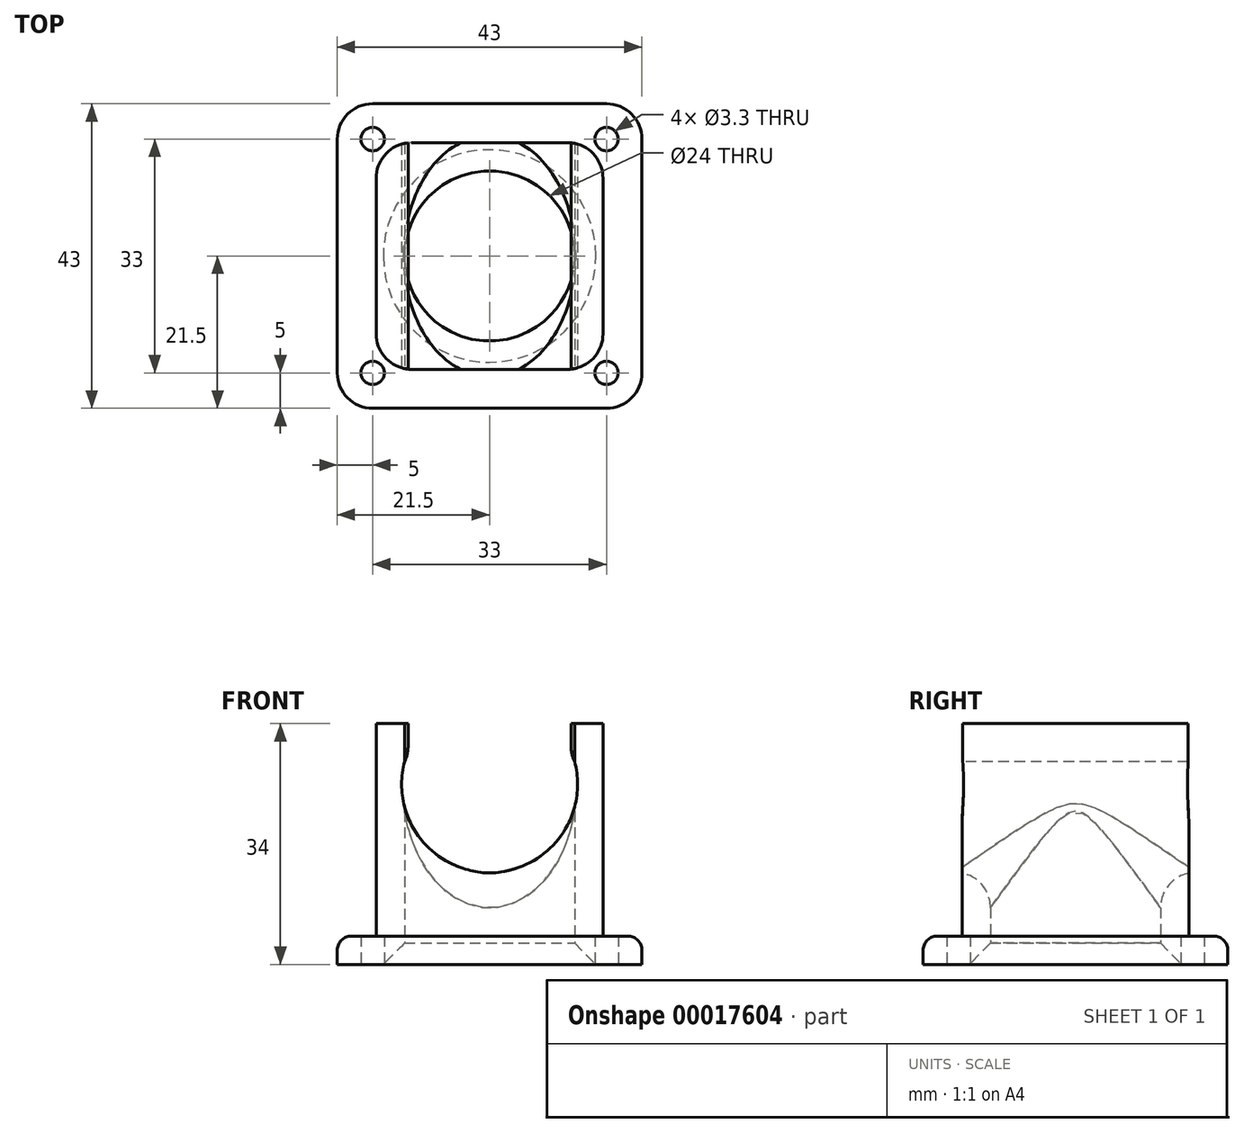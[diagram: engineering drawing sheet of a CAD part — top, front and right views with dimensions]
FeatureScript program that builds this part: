
annotation { "Feature Type Name" : "Feature", "Feature Type Description" : "" }
export const myFeature = defineFeature(function(context is Context, id is Id, definition is map)
    precondition{}
    {
        {
            var Q0;
            Q0=qCreatedBy(makeId("Top.planeOp"),FACE);
            var sketch = newSketch(context, id + "F0", { "sketchPlane" : qUnion([Q0])});
            skLineSegment(sketch, "E0.bottom", {"start": v(0, 0) * mm, "end": v(43, 0) * mm});
            skLineSegment(sketch, "E0.top", {"start": v(0, 43) * mm, "end": v(43, 43) * mm});
            skLineSegment(sketch, "E0.left", {"start": v(0, 0) * mm, "end": v(0, 43) * mm});
            skLineSegment(sketch, "E0.right", {"start": v(43, 0) * mm, "end": v(43, 43) * mm});
            skSolve(sketch);
        }
        {
            var Q0;
            Q0=qSketchRegion(id+"F0",true);
            extrude(context, id + "F1", {"entities" : qUnion([Q0]), "depth" : 4 * mm});
        }
        {
            var Q0;
            Q0=makeQuery(id+"F1.opExtrude","CAP_FACE",FACE,{"disambiguationData":[OSD([sQuery(id+"F0.wireOp",EDGE,"E0.bottom"),sQuery(id+"F0.wireOp",EDGE,"E0.top"),sQuery(id+"F0.wireOp",EDGE,"E0.left"),sQuery(id+"F0.wireOp",EDGE,"E0.right")])],"isStart":false});
            var sketch = newSketch(context, id + "F2", { "sketchPlane" : qUnion([Q0])});
            skLineSegment(sketch, "E1.bottom", {"start": v(5.5, 37.5) * mm, "end": v(37.5, 37.5) * mm});
            skLineSegment(sketch, "E1.top", {"start": v(5.5, 5.5) * mm, "end": v(37.5, 5.5) * mm});
            skLineSegment(sketch, "E1.left", {"start": v(5.5, 37.5) * mm, "end": v(5.5, 5.5) * mm});
            skLineSegment(sketch, "E1.right", {"start": v(37.5, 37.5) * mm, "end": v(37.5, 5.5) * mm});
            skLineSegment(sketch, "E2", {"start": v(21.5, 37.5) * mm, "end": v(21.5, 43) * mm});
            skLineSegment(sketch, "E3", {"start": v(37.5, 21.5) * mm, "end": v(43, 21.5) * mm});
            skSolve(sketch);
        }
        {
            var Q0;
            Q0=qSketchRegion(id+"F2",true);
            extrude(context, id + "F3", {"entities" : qUnion([Q0]), "operationType" : NewBodyOperationType.ADD, "depth" : 30 * mm});
        }
        {
            var Q0;
            Q0=makeQuery(id+"F1.opExtrude","CAP_FACE",FACE,{"disambiguationData":[OSD([sQuery(id+"F0.wireOp",EDGE,"E0.bottom"),sQuery(id+"F0.wireOp",EDGE,"E0.top"),sQuery(id+"F0.wireOp",EDGE,"E0.left"),sQuery(id+"F0.wireOp",EDGE,"E0.right")])],"isStart":true});
            var sketch = newSketch(context, id + "F4", { "sketchPlane" : qUnion([Q0])});
            skCircle(sketch, "E4", {"center": v(21.5, -21.5) * mm, "radius": 18 * mm});
            skLineSegment(sketch, "E5", {"start": v(21.5, -21.5) * mm, "end": v(21.5, 0) * mm});
            skLineSegment(sketch, "E6", {"start": v(21.5, -21.5) * mm, "end": v(43, -21.5) * mm});
            skSolve(sketch);
        }
        {
            var Q0;
            Q0=qSketchRegion(id+"F4",true);
            extrude(context, id + "F5", {"entities" : qUnion([Q0]), "operationType" : NewBodyOperationType.REMOVE, "oppositeDirection" : true, "depth" : 3 * mm});
        }
        {
            var Q0;
            Q0=makeQuery(id+"F5.boolean.opBoolean","COPY",FACE,{"derivedFrom":makeQuery(id+"F5.opExtrude","CAP_FACE",FACE,{"disambiguationData":[OSD([sQuery(id+"F4.wireOp",EDGE,"E4")])],"isStart":false})});
            var sketch = newSketch(context, id + "F6", { "sketchPlane" : qUnion([Q0])});
            skCircle(sketch, "E7", {"center": v(21.5, -21.5) * mm, "radius": 12 * mm});
            skSolve(sketch);
        }
        {
            var Q0;
            Q0=qSketchRegion(id+"F6",true);
            extrude(context, id + "F7", {"entities" : qUnion([Q0]), "operationType" : NewBodyOperationType.REMOVE, "endBound" : BoundingType.THROUGH_ALL, "oppositeDirection" : true, "depth" : 25 * mm});
        }
        {
            var Q0;
            Q0=makeQuery(id+"F3.opExtrude","SWEPT_FACE",FACE,{"disambiguationData":[OSD([sQuery(id+"F2.wireOp",EDGE,"E1.top")])]});
            var sketch = newSketch(context, id + "F8", { "sketchPlane" : qUnion([Q0])});
            skLineSegment(sketch, "E8", {"start": v(9.5, 34) * mm, "end": v(9.5, 28.62) * mm});
            skLineSegment(sketch, "E9", {"start": v(33.5, 34) * mm, "end": v(33.5, 28.62) * mm});
            skLineSegment(sketch, "E10", {"start": v(9.5, 28.62) * mm, "end": v(5.5, 28.62) * mm, "construction": true});
            skLineSegment(sketch, "E11", {"start": v(33.5, 28.62) * mm, "end": v(37.5, 28.62) * mm, "construction": true});
            skCircle(sketch, "E12", {"center": v(21.5, 25.42) * mm, "radius": 12.42 * mm});
            skSolve(sketch);
        }
        {
            var Q0;
            Q0=qSketchRegion(id+"F8",true);
            var Q1;
            {var subQ3=sQuery(id+"F8.wireOp",EDGE,"E8");Q1=makeQuery(id+"F8.imprint","IMPRINT",FACE,{"disambiguationData":[TD([[makeQuery(id+"F8.imprint","IMPRINT",EDGE,{"derivedFrom":subQ3}),1.0]])]});}
            var Q2;
            {var subQ3=sQuery(id+"F8.wireOp",EDGE,"E9");Q2=makeQuery(id+"F8.imprint","IMPRINT",FACE,{"disambiguationData":[TD([[makeQuery(id+"F8.imprint","IMPRINT",EDGE,{"derivedFrom":subQ3}),-1.0]])]});}
            extrude(context, id + "F9", {"entities" : qUnion([Q0, Q1, Q2]), "operationType" : NewBodyOperationType.REMOVE, "endBound" : BoundingType.THROUGH_ALL, "oppositeDirection" : true, "depth" : 25 * mm});
        }
        {
            var Q0;
            Q0=makeQuery(id+"F1.opExtrude","SWEPT_EDGE",EDGE,{"disambiguationData":[OSD([sQuery(id+"F0.wireOp",EDGE,"E0.top"),sQuery(id+"F0.wireOp",EDGE,"E0.right")])]});
            var Q1;
            Q1=makeQuery(id+"F1.opExtrude","SWEPT_EDGE",EDGE,{"disambiguationData":[OSD([sQuery(id+"F0.wireOp",EDGE,"E0.top"),sQuery(id+"F0.wireOp",EDGE,"E0.left")])]});
            var Q2;
            Q2=makeQuery(id+"F1.opExtrude","SWEPT_EDGE",EDGE,{"disambiguationData":[OSD([sQuery(id+"F0.wireOp",EDGE,"E0.bottom"),sQuery(id+"F0.wireOp",EDGE,"E0.left")])]});
            var Q3;
            Q3=makeQuery(id+"F1.opExtrude","SWEPT_EDGE",EDGE,{"disambiguationData":[OSD([sQuery(id+"F0.wireOp",EDGE,"E0.bottom"),sQuery(id+"F0.wireOp",EDGE,"E0.right")])]});
            fillet(context, id + "F10", {"entities" : qUnion([Q0, Q1, Q2, Q3]), "radius" : 5 * mm, "tangentPropagation" : true, "allowEdgeOverflow" : false});
        }
        {
            var Q0;
            Q0=makeQuery(id+"F3.opExtrude","CAP_EDGE",EDGE,{"disambiguationData":[OSD([sQuery(id+"F2.wireOp",EDGE,"E1.bottom")])],"isStart":true});
            var Q1;
            Q1=makeQuery(id+"F3.opExtrude","CAP_EDGE",EDGE,{"disambiguationData":[OSD([sQuery(id+"F2.wireOp",EDGE,"E1.left")])],"isStart":true});
            var Q2;
            Q2=makeQuery(id+"F3.opExtrude","CAP_EDGE",EDGE,{"disambiguationData":[OSD([sQuery(id+"F2.wireOp",EDGE,"E1.top")])],"isStart":true});
            var Q3;
            Q3=makeQuery(id+"F1.opExtrude","CAP_EDGE",EDGE,{"disambiguationData":[OSD([sQuery(id+"F0.wireOp",EDGE,"E0.bottom")])],"isStart":false});
            var Q4;
            Q4=makeQuery(id+"F1.opExtrude","CAP_EDGE",EDGE,{"disambiguationData":[OSD([sQuery(id+"F0.wireOp",EDGE,"E0.left")])],"isStart":false});
            var Q5;
            Q5=makeQuery(id+"F1.opExtrude","CAP_EDGE",EDGE,{"disambiguationData":[OSD([sQuery(id+"F0.wireOp",EDGE,"E0.top")])],"isStart":false});
            fillet(context, id + "F11", {"entities" : qUnion([Q0, Q1, Q2, Q3, Q4, Q5]), "radius" : 2 * mm, "tangentPropagation" : true, "allowEdgeOverflow" : false});
        }
        {
            var Q0;
            Q0=makeQuery(id+"F3.opExtrude","SWEPT_EDGE",EDGE,{"disambiguationData":[OSD([sQuery(id+"F2.wireOp",EDGE,"E1.top"),sQuery(id+"F2.wireOp",EDGE,"E1.left")])]});
            var Q1;
            Q1=makeQuery(id+"F3.opExtrude","SWEPT_EDGE",EDGE,{"disambiguationData":[OSD([sQuery(id+"F2.wireOp",EDGE,"E1.top"),sQuery(id+"F2.wireOp",EDGE,"E1.right")])]});
            var Q2;
            Q2=makeQuery(id+"F3.opExtrude","SWEPT_EDGE",EDGE,{"disambiguationData":[OSD([sQuery(id+"F2.wireOp",EDGE,"E1.bottom"),sQuery(id+"F2.wireOp",EDGE,"E1.right")])]});
            var Q3;
            Q3=makeQuery(id+"F3.opExtrude","SWEPT_EDGE",EDGE,{"disambiguationData":[OSD([sQuery(id+"F2.wireOp",EDGE,"E1.bottom"),sQuery(id+"F2.wireOp",EDGE,"E1.left")])]});
            fillet(context, id + "F12", {"entities" : qUnion([Q0, Q1, Q2, Q3]), "radius" : 5 * mm, "tangentPropagation" : true, "allowEdgeOverflow" : false});
        }
        {
            var Q0;
            {var subQ0=sQuery(id+"F8.wireOp",EDGE,"E12");Q0=makeQuery(id+"F9.boolean.opBoolean","INTERSECT",EDGE,{"derivedFrom":[makeQuery(id+"F7.boolean.opBoolean","COPY",FACE,{"derivedFrom":makeQuery(id+"F7.opExtrude","SWEPT_FACE",FACE,{"disambiguationData":[OSD([sQuery(id+"F6.wireOp",EDGE,"E7")])]})}),makeQuery(id+"F9.opExtrude","SWEPT_FACE",FACE,{"disambiguationData":[OSD([subQ0]),TDD([makeQuery(id+"F8.imprint","IMPRINT",EDGE,{"disambiguationData":[TD([[makeQuery(id+"F8.imprint","INTERSECT",VERTEX,{"derivedFrom":[sQuery(id+"F8.wireOp",EDGE,"E8"),subQ0]}),-1.0]])],"derivedFrom":subQ0})])]})]});}
            fillet(context, id + "F13", {"entities" : qUnion([Q0]), "radius" : 5 * mm, "tangentPropagation" : true, "allowEdgeOverflow" : false});
        }
        {
            var Q0;
            Q0=makeQuery(id+"F1.opExtrude","CAP_FACE",FACE,{"disambiguationData":[OSD([sQuery(id+"F0.wireOp",EDGE,"E0.bottom"),sQuery(id+"F0.wireOp",EDGE,"E0.top"),sQuery(id+"F0.wireOp",EDGE,"E0.left"),sQuery(id+"F0.wireOp",EDGE,"E0.right")])],"isStart":true});
            var sketch = newSketch(context, id + "F14", { "sketchPlane" : qUnion([Q0])});
            skCircle(sketch, "E13", {"center": v(5, -5) * mm, "radius": 1.65 * mm});
            skCircle(sketch, "E14", {"center": v(38, -5) * mm, "radius": 1.65 * mm});
            skCircle(sketch, "E15", {"center": v(38, -38) * mm, "radius": 1.65 * mm});
            skCircle(sketch, "E16", {"center": v(5, -38) * mm, "radius": 1.65 * mm});
            skSolve(sketch);
        }
        {
            var Q0;
            Q0=qSketchRegion(id+"F14",true);
            extrude(context, id + "F15", {"entities" : qUnion([Q0]), "operationType" : NewBodyOperationType.REMOVE, "oppositeDirection" : true, "depth" : 25 * mm});
        }
        {
            var Q0;
            Q0=makeQuery(id+"F5.boolean.opBoolean","COPY",EDGE,{"derivedFrom":makeQuery(id+"F5.opExtrude","CAP_EDGE",EDGE,{"disambiguationData":[OSD([sQuery(id+"F4.wireOp",EDGE,"E4")])],"isStart":false})});
            chamfer(context, id + "F16", {"entities" : qUnion([Q0]), "width" : 6 * mm, "tangentPropagation" : true});
        }
        {
            var Q0;
            Q0=makeQuery(id+"F9.boolean.opBoolean","COPY",FACE,{"derivedFrom":makeQuery(id+"F9.opExtrude","SWEPT_FACE",FACE,{"disambiguationData":[OSD([sQuery(id+"F8.wireOp",EDGE,"E8")])]})});
            var sketch = newSketch(context, id + "F17", { "sketchPlane" : qUnion([Q0])});
            skLineSegment(sketch, "E17.bottom", {"start": v(5.6, 34) * mm, "end": v(37.4, 34) * mm});
            skLineSegment(sketch, "E17.top", {"start": v(5.6, 28.62) * mm, "end": v(37.4, 28.62) * mm});
            skLineSegment(sketch, "E17.left", {"start": v(5.6, 34) * mm, "end": v(5.6, 28.62) * mm});
            skLineSegment(sketch, "E17.right", {"start": v(37.4, 34) * mm, "end": v(37.4, 28.62) * mm});
            skSolve(sketch);
        }
        {
            var Q0;
            Q0=qSketchRegion(id+"F17",true);
            extrude(context, id + "F18", {"entities" : qUnion([Q0]), "operationType" : NewBodyOperationType.ADD, "depth" : 0.5 * mm});
        }
        {
            var Q0;
            Q0=makeQuery(id+"F9.boolean.opBoolean","COPY",FACE,{"derivedFrom":makeQuery(id+"F9.opExtrude","SWEPT_FACE",FACE,{"disambiguationData":[OSD([sQuery(id+"F8.wireOp",EDGE,"E9")])]})});
            var sketch = newSketch(context, id + "F19", { "sketchPlane" : qUnion([Q0])});
            skLineSegment(sketch, "E18.bottom", {"start": v(-37.4, 34) * mm, "end": v(-5.6, 34) * mm});
            skLineSegment(sketch, "E18.top", {"start": v(-37.4, 28.62) * mm, "end": v(-5.6, 28.62) * mm});
            skLineSegment(sketch, "E18.left", {"start": v(-37.4, 34) * mm, "end": v(-37.4, 28.62) * mm});
            skLineSegment(sketch, "E18.right", {"start": v(-5.6, 34) * mm, "end": v(-5.6, 28.62) * mm});
            skSolve(sketch);
        }
        {
            var Q0;
            Q0=qSketchRegion(id+"F19",true);
            extrude(context, id + "F20", {"entities" : qUnion([Q0]), "operationType" : NewBodyOperationType.ADD, "depth" : 0.5 * mm});
        }
        {
            var Q0;
            Q0=makeQuery(id+"F20.opExtrude","CAP_EDGE",EDGE,{"disambiguationData":[OSD([sQuery(id+"F19.wireOp",EDGE,"E18.top")])],"isStart":false});
            var Q1;
            Q1=makeQuery(id+"F18.opExtrude","CAP_EDGE",EDGE,{"disambiguationData":[OSD([sQuery(id+"F17.wireOp",EDGE,"E17.top")])],"isStart":false});
            fillet(context, id + "F21", {"entities" : qUnion([Q0, Q1]), "radius" : 5 * mm, "tangentPropagation" : true, "allowEdgeOverflow" : false});
        }
    });
